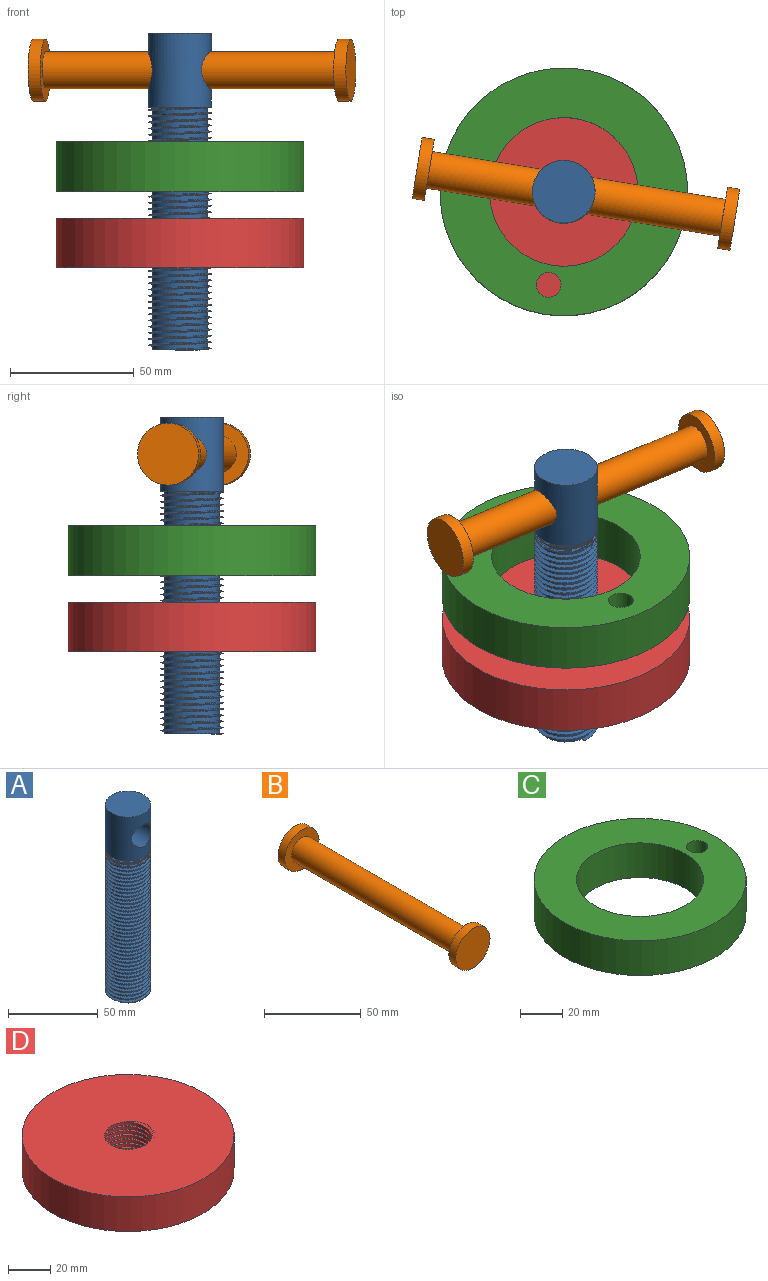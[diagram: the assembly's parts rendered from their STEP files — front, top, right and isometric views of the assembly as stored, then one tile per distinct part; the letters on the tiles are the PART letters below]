
ASSEMBLY  parts=4 mates=3
PART A: 10 faces, bbox 25.9x29.8x129 mm
  f0: cylinder r=12.65mm len=30mm, axis (0,0,-1), area 2003.6mm2, adj f7,f8,f9
  f1: cylinder r=11.14mm len=98mm, axis (0,0,-1), area 5178.4mm2, adj f2,f3,f4,f6,f7
  f2: bspline ~98.73x29.19mm, area 4530.4mm2, adj f1,f3,f6,f7
  f3: bspline ~99.15x29.19mm, area 4560.9mm2, adj f1,f2,f5,f6,f7
  f4: plane 22.39x22.39mm, normal (0,0,-1), area 389.9mm2, adj f1,f5
  f5: bspline ~9.67x5.59mm, area 2.2mm2, adj f3,f4,f6
  f6: plane 1.5x0.8mm, normal (0,-1,-0.04), area 0.6mm2, adj f1,f2,f3,f5
  f7: plane 25.9x25.9mm, normal (0,0,-1), area 95.5mm2, adj f0,f1,f2,f3
  f8: plane 25.3x25.3mm, normal (0,0,1), area 502.9mm2, adj f0
  f9: cylinder r=7.6mm len=25.3mm, axis (0,1,0), area 1208.3mm2, adj f0
PART B: 7 faces, bbox 25x130x25 mm
  f0: cylinder r=7.5mm len=120mm, axis (0,1,0), area 5654.9mm2, adj f3,f6
  f1: cylinder r=12.5mm len=25mm, axis (0,1,0), area 392.7mm2, adj f2,f3
  f2: plane 25x25mm, normal (0,-1,0), area 490.9mm2, adj f1
  f3: plane 25x25mm, normal (0,1,0), area 314.2mm2, adj f0,f1
  f4: cylinder r=12.5mm len=25mm, axis (0,-1,0), area 392.7mm2, adj f5,f6
  f5: plane 25x25mm, normal (0,1,0), area 490.9mm2, adj f4
  f6: plane 25x25mm, normal (0,-1,0), area 314.2mm2, adj f0,f4
PART C: 5 faces, bbox 100x100x20 mm
  f0: plane 100x100mm, normal (0,0,-1), area 4948mm2, adj f2,f3,f4
  f1: plane 100x100mm, normal (0,0,1), area 4948mm2, adj f2,f3,f4
  f2: cylinder r=50mm len=100mm, axis (0,0,1), area 6283.2mm2, adj f0,f1
  f3: cylinder r=30mm len=60mm, axis (0,0,1), area 3769.9mm2, adj f0,f1
  f4: cylinder r=5mm len=20mm, axis (0,0,1), area 628.3mm2, adj f0,f1
PART D: 6 faces, bbox 100x100x21.2 mm
  f0: plane 100x100mm, normal (0,0,1), area 7446.6mm2, adj f2,f3,f4,f5
  f1: plane 100x100mm, normal (0,0,-1), area 7446.6mm2, adj f2,f3,f4,f5
  f2: cylinder r=50mm len=100mm, axis (0,0,-1), area 6283.2mm2, adj f0,f1
  f3: cylinder r=11.14mm len=22.28mm, axis (0,0,-1), area 928mm2, adj f0,f1,f4,f5
  f4: bspline ~29.19x25.28mm, area 931.2mm2, adj f0,f1,f3,f5
  f5: bspline ~29.19x25.28mm, area 931.4mm2, adj f0,f1,f3,f4
PLACE A rot(axis=(0,0,-1),99.3deg) t=(0,0,-33.19)mm
PLACE B rot(axis=(0,0,-1),99.3deg) t=(4.93,-0.8,-33.19)mm
PLACE C rot(axis=(0,0,-1),99.3deg) t=(0,0,-43.19)mm
PLACE D at identity fixed
MATE slider B.f0 <-> A.f9  axis (0.99,-0.16,0) through (4.93,-0.8,69.81)mm
MATE revolute A.f0 <-> C.f2  axis (0,0,1) through (0,0,40.81)mm
MATE cylindrical D.f2 <-> A.f0  axis (0,0,-1) through (0,0,-10)mm
